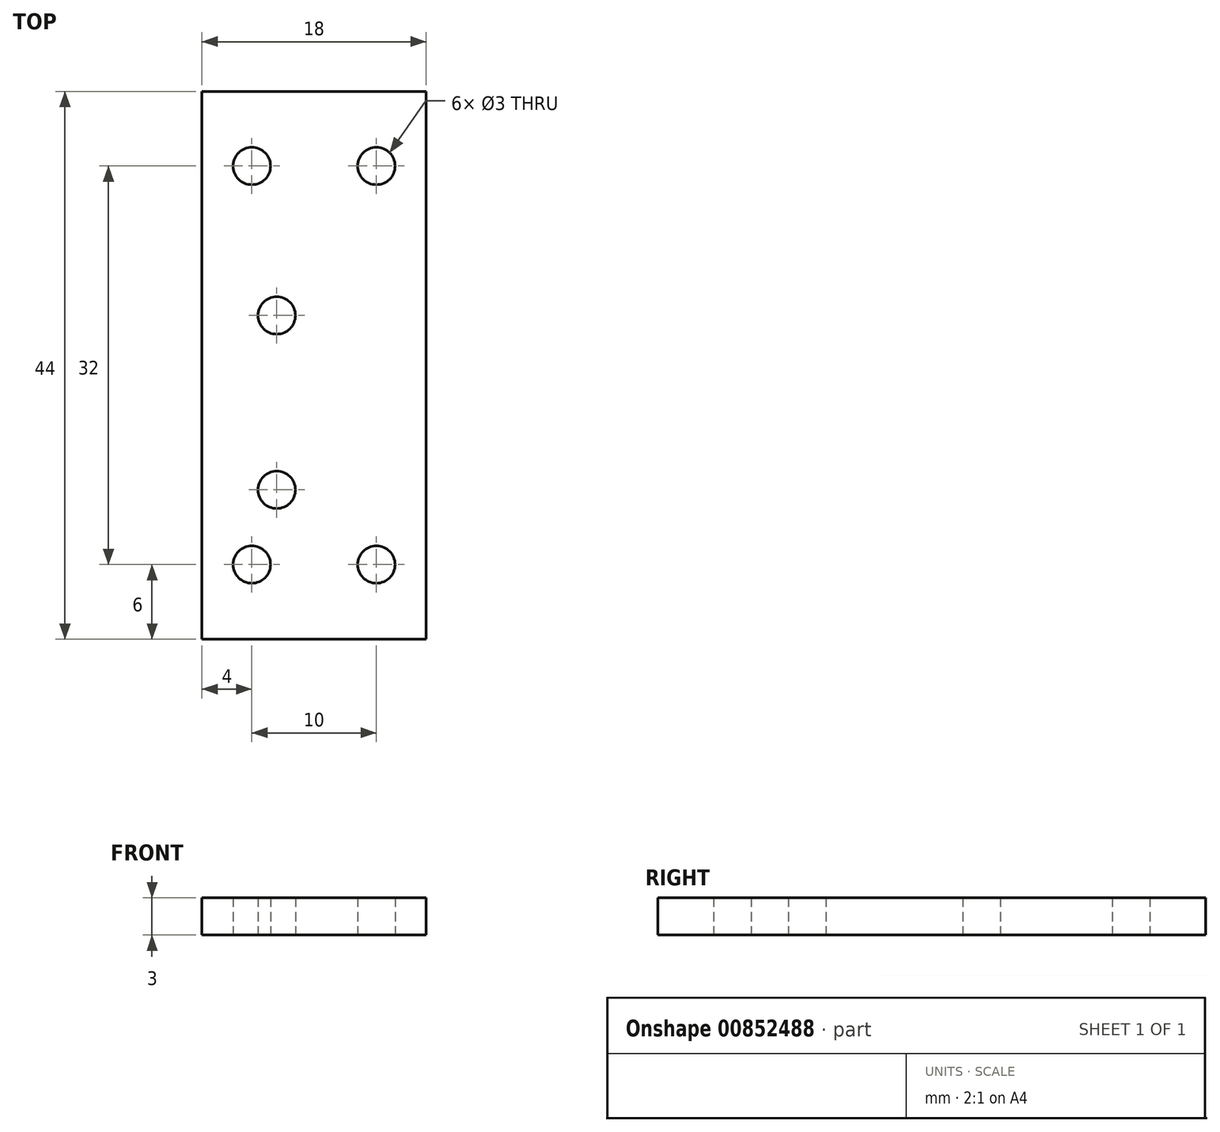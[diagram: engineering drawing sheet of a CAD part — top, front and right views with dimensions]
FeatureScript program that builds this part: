
annotation { "Feature Type Name" : "Feature", "Feature Type Description" : "" }
export const myFeature = defineFeature(function(context is Context, id is Id, definition is map)
    precondition{}
    {
        {
            var Q0;
            Q0=qCreatedBy(makeId("Top.planeOp"),FACE);
            var sketch = newSketch(context, id + "F0", { "sketchPlane" : qUnion([Q0])});
            skLineSegment(sketch, "E0.bottom", {"start": v(9, -22) * mm, "end": v(-9, -22) * mm});
            skLineSegment(sketch, "E0.top", {"start": v(9, 22) * mm, "end": v(-9, 22) * mm});
            skLineSegment(sketch, "E0.left", {"start": v(9, -22) * mm, "end": v(9, 22) * mm});
            skLineSegment(sketch, "E0.right", {"start": v(-9, -22) * mm, "end": v(-9, 22) * mm});
            skPoint(sketch, "E0.middle", {"position": v(0, 0) * mm});
            skLineSegment(sketch, "E1.bottom", {"start": v(5, -16) * mm, "end": v(-5, -16) * mm});
            skLineSegment(sketch, "E1.top", {"start": v(5, 16) * mm, "end": v(-5, 16) * mm});
            skLineSegment(sketch, "E1.left", {"start": v(5, -16) * mm, "end": v(5, 16) * mm});
            skLineSegment(sketch, "E2", {"start": v(-3, 4) * mm, "end": v(-3, -10) * mm});
            skSolve(sketch);
        }
        {
            var Q0;
            Q0=makeQuery(id+"F0.imprint","IMPRINT",FACE,{"disambiguationData":[TD([[makeQuery(id+"F0.imprint","IMPRINT",EDGE,{"derivedFrom":sQuery(id+"F0.wireOp",EDGE,"E0.bottom")}),-1.0]])]});
            var Q1;
            Q1=makeQuery(id+"F0.imprint","IMPRINT",FACE,{"disambiguationData":[TD([[makeQuery(id+"F0.imprint","IMPRINT",EDGE,{"derivedFrom":sQuery(id+"F0.wireOp",EDGE,"E1.bottom")}),-1.0]])]});
            extrude(context, id + "F1", {"entities" : qUnion([Q0, Q1]), "depth" : 3 * mm, "offsetDistance" : 25 * mm});
        }
        {
            var Q0;
            Q0=sQuery(id+"F0.wireOp",VERTEX,"E1.right.start");
            var Q1;
            Q1=sQuery(id+"F0.wireOp",VERTEX,"E1.top.end");
            var Q2;
            Q2=sQuery(id+"F0.wireOp",VERTEX,"ozUQODt5-Zu5h-IEne-2nYX-yZyh12t1jf9q.left.start");
            var Q3;
            Q3=sQuery(id+"F0.wireOp",VERTEX,"ozUQODt5-Zu5h-IEne-2nYX-yZyh12t1jf9q.left.end");
            var Q4;
            Q4=sQuery(id+"F0.wireOp",VERTEX,"E1.bottom.start");
            var Q5;
            Q5=sQuery(id+"F0.wireOp",VERTEX,"E1.top.start");
            var Q6;
            Q6=sQuery(id+"F0.wireOp",VERTEX,"E1.bottom.end");
            var Q7;
            Q7=sQuery(id+"F0.wireOp",VERTEX,"E2.end");
            var Q8;
            Q8=sQuery(id+"F0.wireOp",VERTEX,"E2.start");
            var Q9;
            Q9=makeQuery(id+"F1.opExtrude","SWEPT_BODY",BODY,{"disambiguationData":[OSD([sQuery(id+"F0.wireOp",EDGE,"E0.bottom"),sQuery(id+"F0.wireOp",EDGE,"E0.top"),sQuery(id+"F0.wireOp",EDGE,"E0.left"),sQuery(id+"F0.wireOp",EDGE,"E0.right")])]});
            hole(context, id + "F2", {"style" : HoleStyle.SIMPLE, "endStyle" : HoleEndStyle.THROUGH, "oppositeDirection" : true, "holeDiameter" : 3 * mm, "majorDiameter" : 5 * mm, "isTappedThrough" : true, "tappedDepth" : 12 * mm, "tapClearance" : 3, "locations" : qUnion([Q0, Q1, Q2, Q3, Q4, Q5, Q6, Q7, Q8]), "scope" : qUnion([Q9])});
        }
    });
